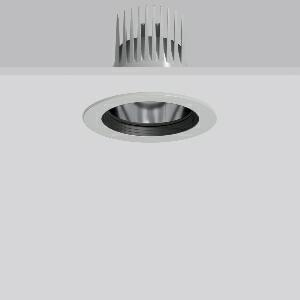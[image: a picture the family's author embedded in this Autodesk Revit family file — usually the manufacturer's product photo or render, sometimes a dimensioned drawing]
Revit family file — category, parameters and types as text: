
# Revit family: heledon_maxi_e_901759_004_3_76_6c9e
name_source: partatom
category: Lighting Fixtures
units: mm (PartAtom-declared; Revit-internal decimal feet)

## family parameters
Cut with Voids When Loaded = No
Host = Face
Light Source = No
Part Type = Normal
Room Calculation Point = No
Round Connector Dimension = Use Diameter
Shared = No

## types (1)
- HELEDON maxi E (1 x LED Modul 935, 3250 lm, 3500)
    Apparent Load = 25 VA
    Approval mark = CE
    CIE Flux Codes = 97 100 100 100 100
    Color Rendering = 92
    Color Temperature = 3500
    Default Elevation = 1800 mm
    Description = Series: HELEDON maxi
Round recessed downlight. Housing: die-cast aluminium, powder-coated. Black plastic ring and recessed LED to prevent glare from the side. Optical assembly with reflector made of MIRO-Silver with 98% total light reflection for outstanding efficiency - can be changed without tools. Best colour rendering index Ra>90. Suitable for Recessed ceiling mounting. Installation without tools thanks to spring fastening system. Including separate LED converter with connecting cable 600 mm.High quality converter without flickering and stroboscopic effect. Through-wiring box (5 pole) available as accessory. The following accessories can be mounted without use of tools: interchangeable lenses, decorative glasses, honeycomb louvre, clear and frosted diffusers, white interchangeable plastic ring. 
Colour: silver
Diameter: 162 mm
Height: 3 mm
Cut-out diameter: 152 mm
Recess height: 200 mm
Luminaire: recess height: 135 mm
Lamp: LED
Socket: without socket
Colour temperature: 3500K
Colour rendering index (CRI): 92
System power: 25 W
Rated luminous flux: 3250 lm
Luminous efficiency: 130 lm/W
Control gear: Converter, dimmable, DALI
Protection class: II
Type of protection: IP 20
    Height = 0 mm  [stored 0 ft]
    Lamp = 1 x LED Modul 935
    Lamp Light Flux = 3250 lm
    Lamp count = 1
    Length = 162 mm
    Lifetime = 50000 h
    Luminous efficacy = 130 lm/W
    Manufacturer = RZB
    ModVariant = No
    Model = 901759.004.3.76
    Mounting Place = Ceiling
    Mounting Type = Recessed
    Number of Poles = 1
    OnlyDefault = Yes
    Power Factor = 1
    Product Name = HELEDON maxi E
    Product group = Recessed downlights
    ProductGroupID = 402
    Protection Class = Protection class II
    Protection Degree = IP 20
    RLX_Detail_Level = 1
    RLX_Emergency_Light_Flux = 0 lm
    RLX_Emergency_Type = 0
    RLX_Emergency_Type_DB = No
    RlxData = <blob elided: 119665 chars, md5=8fa788b8>
    Socket = socket
    Standby Power = 0 W
    System Light Flux = 3250 lm
    System Power = 25 W
    Type Comments = Product without accessories
    Type Image = 901662.004.jpg
    URL = http://relux.com
    VarID = ---
    Voltage = 230 V
    Voltage Range = 220-240 V
    Weight = 0.00 kg
    Width = 0 mm  [stored 0 ft]

note: [stored X ft] marks values corroborated as IEEE doubles in the binary element streams (Revit-internal decimal feet)

## geometry (parser evidence)
native form markers: Blend x4, Sweep x12
no freeform markers — native parametric forms only
